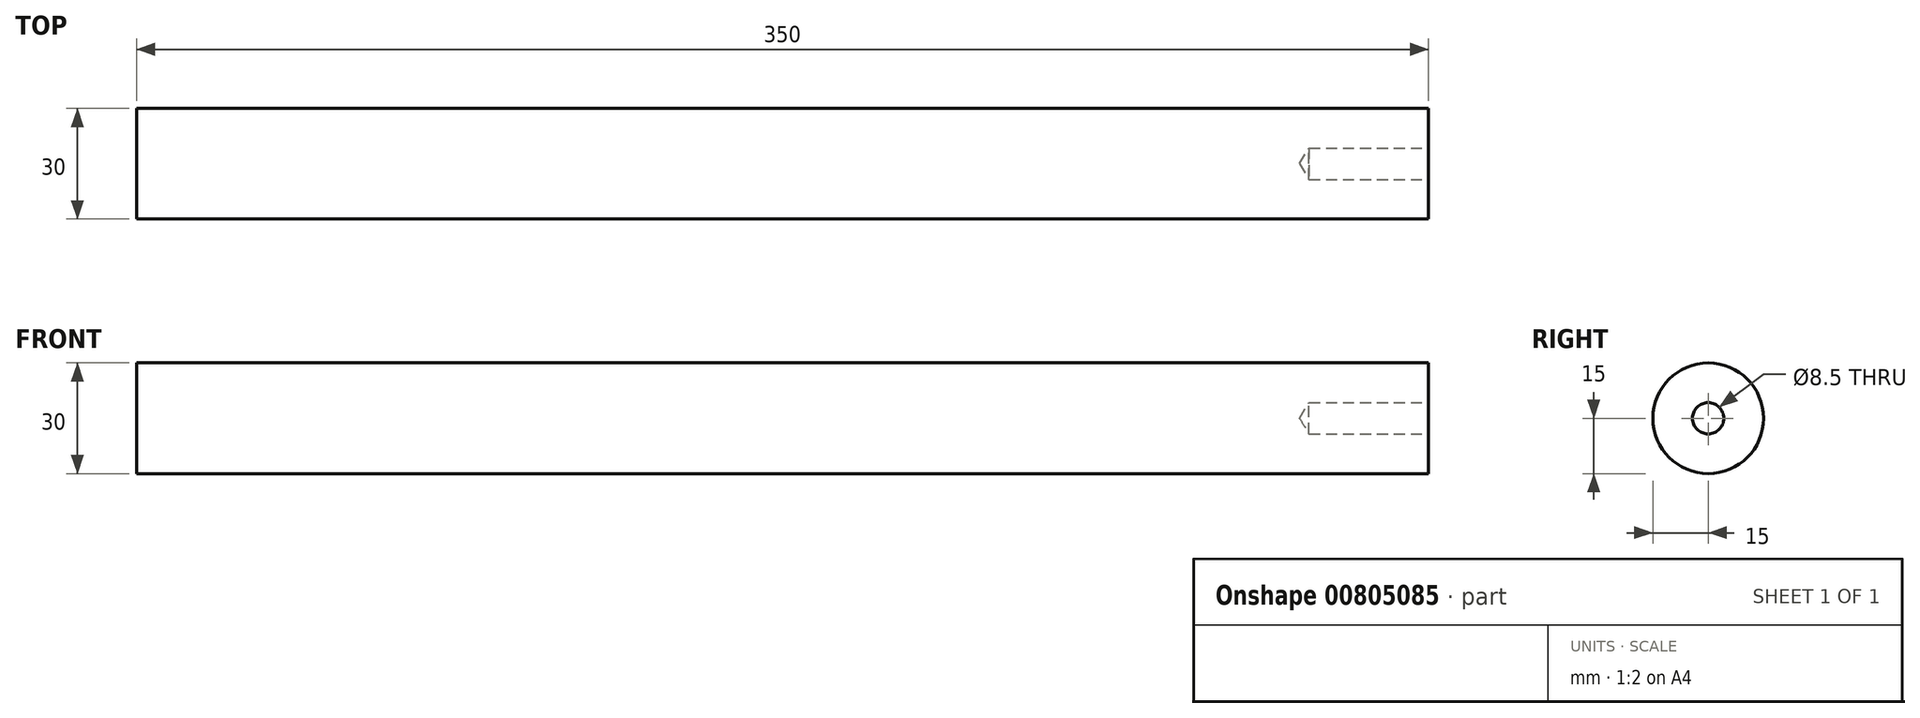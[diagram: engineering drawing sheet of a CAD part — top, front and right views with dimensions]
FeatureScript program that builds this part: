
annotation { "Feature Type Name" : "Feature", "Feature Type Description" : "" }
export const myFeature = defineFeature(function(context is Context, id is Id, definition is map)
    precondition{}
    {
        {
            var Q0;
            Q0=qCreatedBy(makeId("Right.planeOp"),FACE);
            var sketch = newSketch(context, id + "F0", { "sketchPlane" : qUnion([Q0])});
            skCircle(sketch, "E0", {"center": v(0, 0) * mm, "radius": 15 * mm});
            skSolve(sketch);
        }
        {
            var Q0;
            Q0 = qSketchRegion(id + "F0", true);
            extrude(context, id + "F1", {"entities" : qUnion([Q0]), "depth" : 350 * mm, "offsetDistance" : 25 * mm});
        }
        {
            var Q0;
            Q0=makeQuery(id+"F1.opExtrude","CAP_FACE",FACE,{"disambiguationData":[OSD([sQuery(id+"F0.wireOp",EDGE,"E0")])],"isStart":false});
            var sketch = newSketch(context, id + "F2", { "sketchPlane" : qUnion([Q0])});
            skPoint(sketch, "E1", {"position": v(0, 0) * mm});
            skSolve(sketch);
        }
        {
            var Q0;
            Q0=sQuery(id+"F2.wireOp",VERTEX,"E1");
            var Q1;
            Q1=makeQuery(id+"F1.opExtrude","SWEPT_BODY",BODY,{"disambiguationData":[OSD([sQuery(id+"F0.wireOp",EDGE,"E0")])]});
            hole(context, id + "F3", {"style" : HoleStyle.SIMPLE, "endStyle" : HoleEndStyle.BLIND, "standardTappedOrClearance" : lookupTablePath({ "standard" : "ISO", "engagement" : "75%", "pitch" : "1.5 mm", "size" : "M10", "type" : "Tapped" }), "standardBlindInLast" : lookupTablePath({ "standard" : "ISO", "engagement" : "75%", "pitch" : "1.5 mm", "size" : "M10", "type" : "Tapped" }), "holeDiameter" : 8.5 * mm, "majorDiameter" : 10 * mm, "showTappedDepth" : true, "holeDepth" : 32.4 * mm, "isTappedThrough" : true, "tappedDepth" : 27.9 * mm, "tapClearance" : 3, "startFromSketch" : true, "locations" : qUnion([Q0]), "scope" : qUnion([Q1])});
        }
        {
            var Q0;
            Q0=qCreatedBy(makeId("Top.planeOp"),FACE);
            cPlane(context, id + "F4", {"entities" : qUnion([Q0]), "cplaneType" : CPlaneType.OFFSET, "offset" : 15 * mm, "width" : 150 * mm, "height" : 150 * mm});
        }
    });
